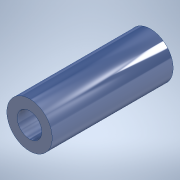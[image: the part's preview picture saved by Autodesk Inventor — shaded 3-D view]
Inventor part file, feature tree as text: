
AUTODESK INVENTOR PART (.ipt)
format: ipt  version: 2020 (Build 240168000, 168)  size: 105,472 bytes
history: native  units: in
note: dims shown in document units (in); Inventor stores cm internally (conversion verified against a paired STEP export)
features: extrude x1, sketch x1
ambient origin geometry x8: Origin, YZ Plane, XZ Plane, XY Plane, X Axis, Y Axis, Z Axis, Center Point
bodies: Solid1 (feature_tree)
feature tree (2):
  extrude  "Extrusion1"  Depth=1.0in
  sketch  "Sketch1"  dims[d0=0.203in d1=0.375in d2=1.0in d3=0.0in]
